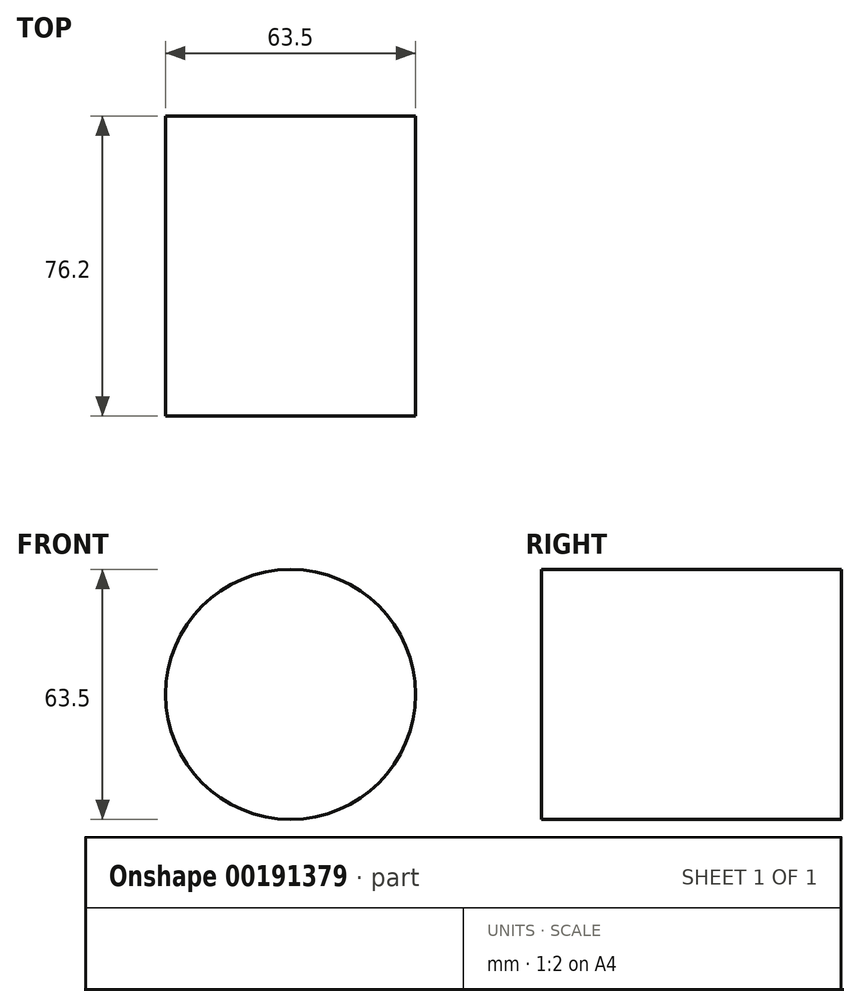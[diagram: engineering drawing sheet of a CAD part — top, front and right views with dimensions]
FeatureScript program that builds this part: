
annotation { "Feature Type Name" : "Feature", "Feature Type Description" : "" }
export const myFeature = defineFeature(function(context is Context, id is Id, definition is map)
    precondition{}
    {
        {
            var Q0;
            Q0=qCreatedBy(makeId("Front.planeOp"),FACE);
            var sketch = newSketch(context, id + "F0", { "sketchPlane" : qUnion([Q0])});
            skCircle(sketch, "E0", {"center": v(0, 0) * mm, "radius": 31.75 * mm});
            skSolve(sketch);
        }
        {
            var Q0;
            Q0=makeQuery(id+"F0.imprint","IMPRINT",FACE,{"disambiguationData":[TD([[makeQuery(id+"F0.imprint","IMPRINT",EDGE,{"derivedFrom":sQuery(id+"F0.wireOp",EDGE,"E0")}),1.0]])]});
            extrude(context, id + "F1", {"entities" : qUnion([Q0]), "depth" : 76.2 * mm});
        }
    });
